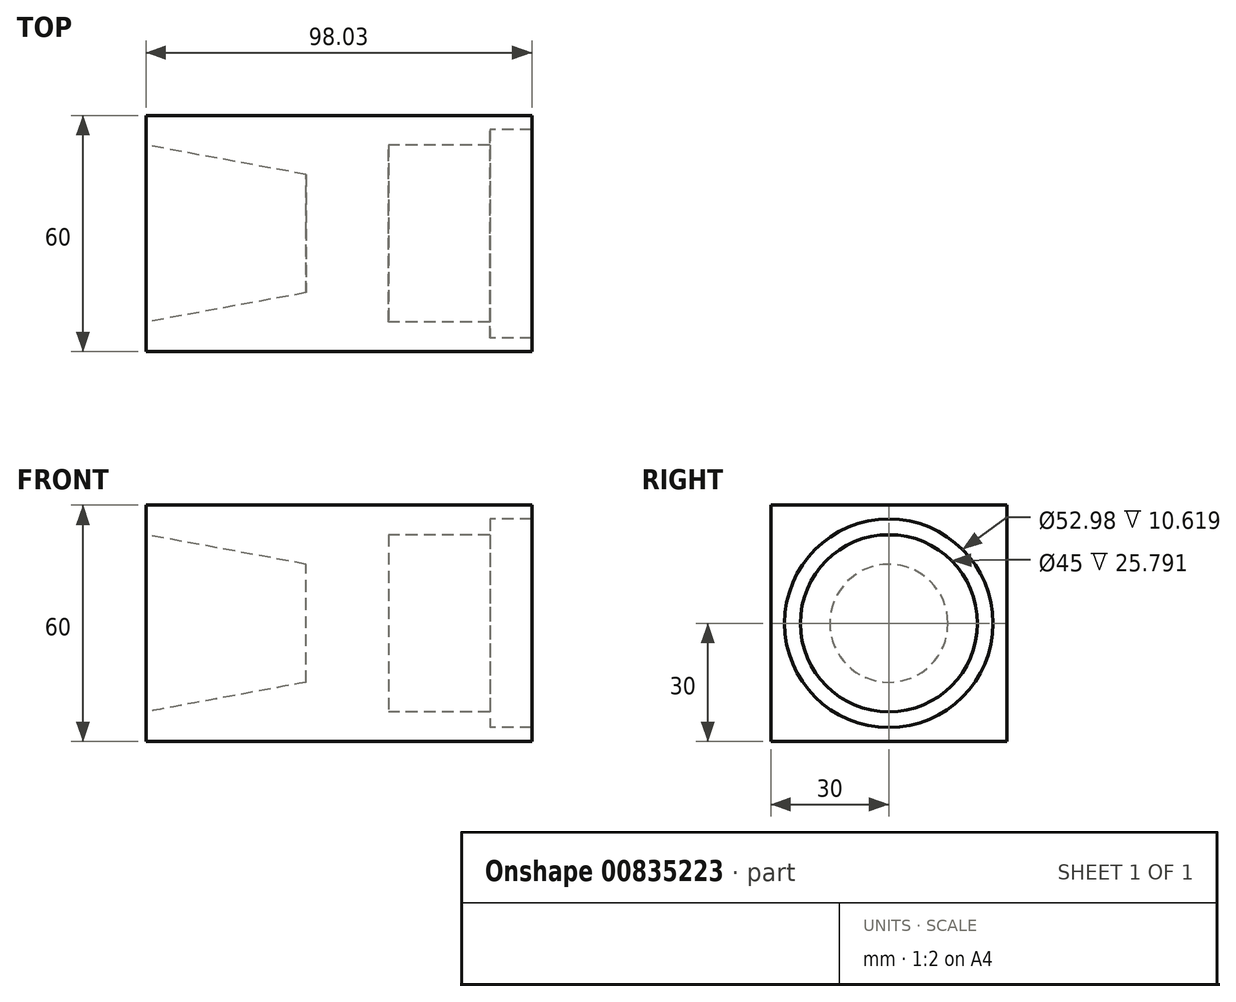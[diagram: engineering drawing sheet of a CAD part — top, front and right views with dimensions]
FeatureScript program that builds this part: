
annotation { "Feature Type Name" : "Feature", "Feature Type Description" : "" }
export const myFeature = defineFeature(function(context is Context, id is Id, definition is map)
    precondition{}
    {
        {
            var Q0;
            Q0=qCreatedBy(makeId("Front.planeOp"),FACE);
            var sketch = newSketch(context, id + "F0", { "sketchPlane" : qUnion([Q0])});
            skLineSegment(sketch, "E0", {"start": v(-67.39, 0) * mm, "end": v(54.1, 0) * mm, "construction": true});
            skLineSegment(sketch, "E1", {"start": v(-61.62, 22.5) * mm, "end": v(-61.62, -22.5) * mm});
            skPoint(sketch, "E2", {"position": v(-61.62, 0) * mm});
            skLineSegment(sketch, "E3", {"start": v(-20.9, 15) * mm, "end": v(-61.62, 22.5) * mm});
            skLineSegment(sketch, "E4", {"start": v(-20.9, -15) * mm, "end": v(-61.62, -22.5) * mm});
            skLineSegment(sketch, "E5", {"start": v(-20.9, -15) * mm, "end": v(-20.9, 0) * mm});
            skLineSegment(sketch, "E6", {"start": v(-61.62, 22.5) * mm, "end": v(-61.62, 30) * mm});
            skLineSegment(sketch, "E7", {"start": v(-61.62, 30) * mm, "end": v(0, 30) * mm});
            skLineSegment(sketch, "E8", {"start": v(0, 30) * mm, "end": v(0, 22.5) * mm, "construction": true});
            skLineSegment(sketch, "E9", {"start": v(0, -30) * mm, "end": v(-61.62, -30) * mm});
            skLineSegment(sketch, "E10", {"start": v(-61.62, -30) * mm, "end": v(-61.62, -22.5) * mm});
            skLineSegment(sketch, "E11", {"start": v(0, 30) * mm, "end": v(36.41, 30) * mm});
            skLineSegment(sketch, "E12", {"start": v(36.41, 30) * mm, "end": v(36.41, 22.5) * mm});
            skLineSegment(sketch, "E13", {"start": v(36.41, 22.5) * mm, "end": v(0, 22.5) * mm});
            skLineSegment(sketch, "E14", {"start": v(0, -30) * mm, "end": v(36.41, -30) * mm});
            skLineSegment(sketch, "E15", {"start": v(36.41, -30) * mm, "end": v(36.41, -22.5) * mm});
            skLineSegment(sketch, "E16", {"start": v(36.41, -22.5) * mm, "end": v(0, -22.5) * mm});
            skLineSegment(sketch, "E17", {"start": v(36.41, -22.5) * mm, "end": v(36.41, 22.5) * mm});
            skLineSegment(sketch, "E18", {"start": v(0, 22.5) * mm, "end": v(0, -22.5) * mm});
            skLineSegment(sketch, "E19", {"start": v(0, -22.5) * mm, "end": v(0, -30) * mm, "construction": true});
            skLineSegment(sketch, "E20", {"start": v(-20.9, 0) * mm, "end": v(-20.9, 15) * mm});
            skLineSegment(sketch, "E21", {"start": v(-61.62, 0) * mm, "end": v(-20.9, 0) * mm});
            skLineSegment(sketch, "E22", {"start": v(0, 0) * mm, "end": v(36.41, 0) * mm});
            skLineSegment(sketch, "E23", {"start": v(25.8, 22.5) * mm, "end": v(25.8, 26.49) * mm});
            skLineSegment(sketch, "E24", {"start": v(25.8, 26.49) * mm, "end": v(36.41, 26.49) * mm});
            skLineSegment(sketch, "E25", {"start": v(25.8, -22.5) * mm, "end": v(25.8, -26.49) * mm});
            skLineSegment(sketch, "E26", {"start": v(25.8, -26.49) * mm, "end": v(36.41, -26.49) * mm});
            skLineSegment(sketch, "E27", {"start": v(25.8, 22.5) * mm, "end": v(25.8, -22.5) * mm});
            skSolve(sketch);
        }
        {
            var Q0;
            Q0=makeQuery(id+"F0.imprint","IMPRINT",FACE,{"disambiguationData":[TD([[makeQuery(id+"F0.imprint","IMPRINT",EDGE,{"derivedFrom":sQuery(id+"F0.wireOp",EDGE,"E3")}),-1.0]])]});
            var Q1;
            Q1=makeQuery(id+"F0.imprint","IMPRINT",FACE,{"disambiguationData":[TD([[makeQuery(id+"F0.imprint","IMPRINT",EDGE,{"derivedFrom":sQuery(id+"F0.wireOp",EDGE,"E13")}),1.0]])]});
            var Q2;
            Q2=makeQuery(id+"F0.imprint","IMPRINT",FACE,{"disambiguationData":[TD([[makeQuery(id+"F0.imprint","IMPRINT",EDGE,{"derivedFrom":sQuery(id+"F0.wireOp",EDGE,"E1")}),1.0]])]});
            var Q3;
            {var subQ0=sQuery(id+"F0.wireOp",EDGE,"E16");Q3=makeQuery(id+"F0.imprint","IMPRINT",FACE,{"disambiguationData":[TD([[makeQuery(id+"F0.imprint","IMPRINT",EDGE,{"derivedFrom":subQ0}),-1.0]])]});}
            var Q4;
            {var subQ4=sQuery(id+"F0.wireOp",EDGE,"E23");Q4=makeQuery(id+"F0.imprint","IMPRINT",FACE,{"disambiguationData":[TD([[makeQuery(id+"F0.imprint","IMPRINT",EDGE,{"derivedFrom":subQ4}),-1.0]])]});}
            var Q5;
            {var subQ4=sQuery(id+"F0.wireOp",EDGE,"E25");Q5=makeQuery(id+"F0.imprint","IMPRINT",FACE,{"disambiguationData":[TD([[makeQuery(id+"F0.imprint","IMPRINT",EDGE,{"derivedFrom":subQ4}),1.0]])]});}
            extrude(context, id + "F1", {"entities" : qUnion([Q0, Q1, Q2, Q3, Q4, Q5]), "endBound" : BoundingType.SYMMETRIC, "depth" : 60 * mm, "offsetDistance" : 25 * mm});
        }
        {
            var Q0;
            {var subQ0=sQuery(id+"F0.wireOp",EDGE,"E4");Q0=makeQuery(id+"F0.imprint","IMPRINT",FACE,{"disambiguationData":[TD([[makeQuery(id+"F0.imprint","IMPRINT",EDGE,{"derivedFrom":subQ0}),-1.0]])]});}
            var Q1;
            Q1=sQuery(id+"F0.wireOp",EDGE,"E0");
            revolve(context, id + "F2", {"operationType" : NewBodyOperationType.REMOVE, "surfaceOperationType" : NewSurfaceOperationType.NEW, "entities" : qUnion([Q0]), "axis" : qUnion([Q1]), "revolveType" : RevolveType.FULL, "oppositeDirection" : true});
        }
        {
            var Q0;
            {var subQ0=sQuery(id+"F0.wireOp",EDGE,"E13");Q0=makeQuery(id+"F0.imprint","IMPRINT",FACE,{"disambiguationData":[TD([[makeQuery(id+"F0.imprint","IMPRINT",EDGE,{"derivedFrom":subQ0}),1.0]])]});}
            var Q1;
            {var subQ4=sQuery(id+"F0.wireOp",EDGE,"E23");Q1=makeQuery(id+"F0.imprint","IMPRINT",FACE,{"disambiguationData":[TD([[makeQuery(id+"F0.imprint","IMPRINT",EDGE,{"derivedFrom":subQ4}),-1.0]])]});}
            var Q2;
            Q2=sQuery(id+"F0.wireOp",EDGE,"E0");
            revolve(context, id + "F3", {"operationType" : NewBodyOperationType.REMOVE, "surfaceOperationType" : NewSurfaceOperationType.NEW, "entities" : qUnion([Q0, Q1]), "axis" : qUnion([Q2]), "revolveType" : RevolveType.FULL});
        }
    });
